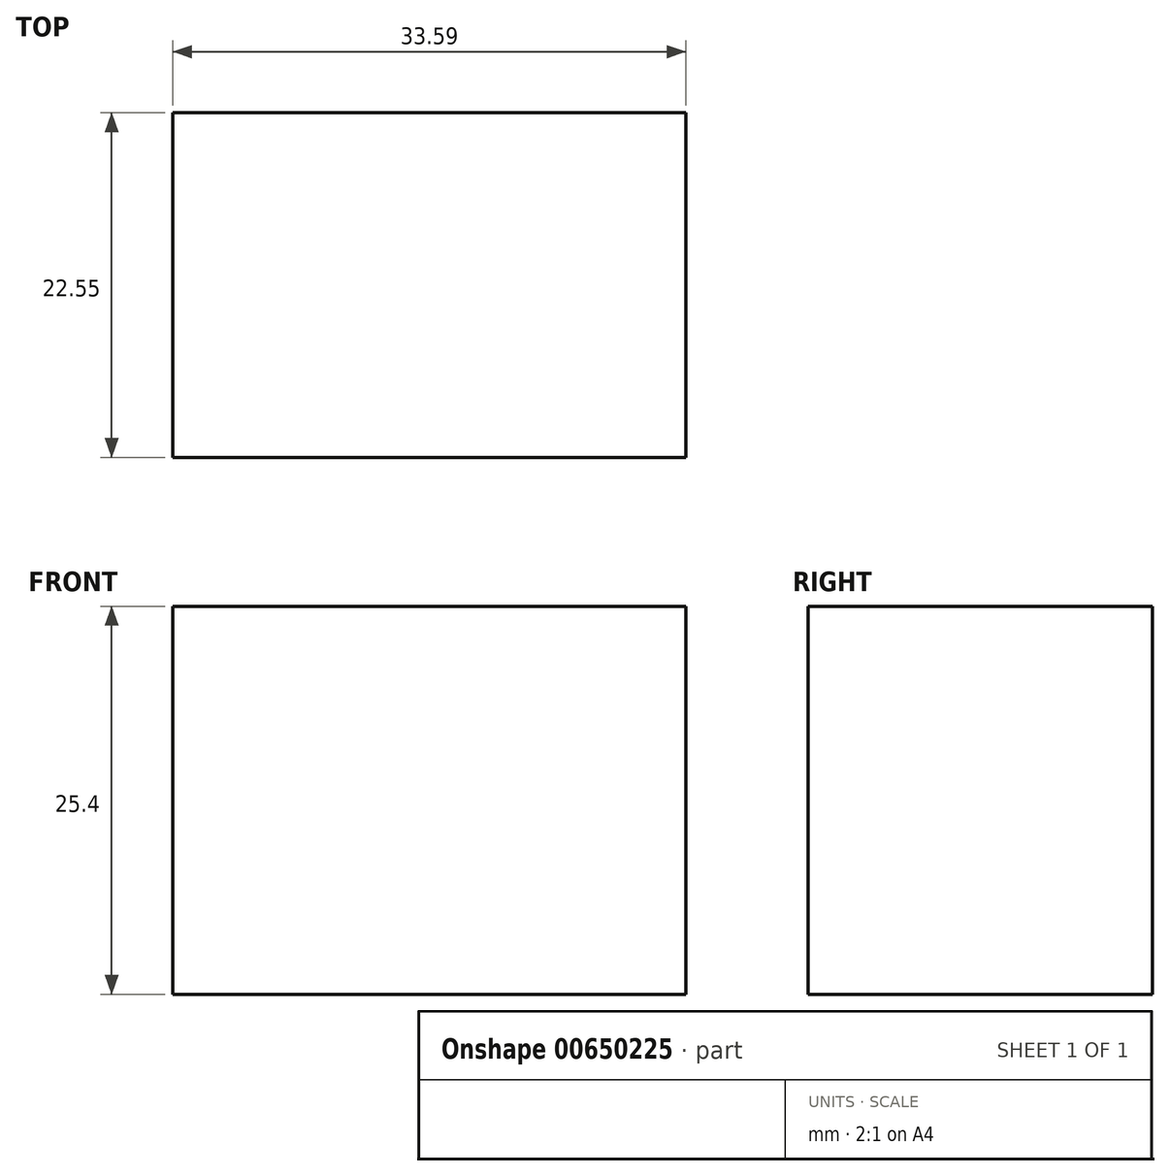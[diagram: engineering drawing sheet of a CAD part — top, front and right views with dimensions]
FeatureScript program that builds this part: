
annotation { "Feature Type Name" : "Feature", "Feature Type Description" : "" }
export const myFeature = defineFeature(function(context is Context, id is Id, definition is map)
    precondition{}
    {
        {
            var Q0;
            Q0=qCreatedBy(makeId("Top.planeOp"),FACE);
            var sketch = newSketch(context, id + "F0", { "sketchPlane" : qUnion([Q0])});
            skLineSegment(sketch, "E0", {"start": v(0, 0) * mm, "end": v(33.59, 0) * mm});
            skLineSegment(sketch, "E1", {"start": v(33.59, 0) * mm, "end": v(33.59, 22.55) * mm});
            skLineSegment(sketch, "E2", {"start": v(33.59, 22.55) * mm, "end": v(0, 22.55) * mm});
            skLineSegment(sketch, "E3", {"start": v(0, 22.55) * mm, "end": v(0, 0) * mm});
            skSolve(sketch);
        }
        {
            var Q0;
            Q0 = qSketchRegion(id + "F0", true);
            extrude(context, id + "F1", {"entities" : qUnion([Q0]), "depth" : 25.4 * mm, "offsetDistance" : 25.4 * mm});
        }
    });
